# Revit family: FK037-18x15.5xX-Z
name_source: partatom
category: Furniture
units: mm (PartAtom-declared; Revit-internal decimal feet)

## family parameters
Always vertical = Yes
Cut with Voids When Loaded = No
OmniClass Number = 23.40.20.00
OmniClass Title = General Furniture and Specialties
Room Calculation Point = No
Shared = No
Work Plane-Based = No

## types (2) — shared parameters
Length = 3' - 4"
Manufacturer = Fomcore
Seat = <By Category>
Side = <By Category>
Type Comments = Lilypad Series
URL = https://fomcore.com
Width = 0' - 10"

## per-type parameters (varying)
| type | Description | hEIGHT |
| FK037-18x15.5x3-Z | 3" Hexy Lily Pad, 18"Lx15.5"Wx3"H, Zippered (Minimum Order of 10 Quantity) | 0' - 3" |
| FK037-18x15.5x6-Z | 6" Hexy Lily Pad, 18"Lx15.5"Wx6"H, Zippered (Minimum Order of 5 Quantity) | 0' - 6" |

note: column(s) folded — value = type name in every type: Model

## geometry (parser evidence)
native form markers: Sweep x3
no freeform markers — native parametric forms only
